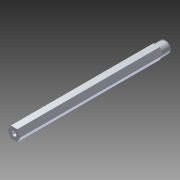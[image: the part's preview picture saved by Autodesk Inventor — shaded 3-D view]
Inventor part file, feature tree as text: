
AUTODESK INVENTOR PART (.ipt)
format: ipt  version: 2015 SP1 (Build 190203100, 203)  size: 120,832 bytes
history: native  units: in
note: dims shown in document units (in); Inventor stores cm internally (conversion verified against a paired STEP export)
features: other x2, extrude x1, imported_body x1, sketch x1, projected_geometry x1
ambient origin geometry x8: Origin, YZ Plane, XZ Plane, XY Plane, X Axis, Y Axis, Z Axis, Center Point
bodies: Body1 (feature_tree)
feature tree (6):
  other  "1_4-20 Tapped Hole1"
  other  "217-3421-004 Rev1.ipt1"
  extrude  "Extrusion1"  Depth=0.125in TaperAngle=0.0deg
  imported_body  "Base1"
  sketch  "Sketch1"  dims[d0=0.6in d1=0.125in d2=0.0in]
  projected_geometry  "Projected Loop1"
